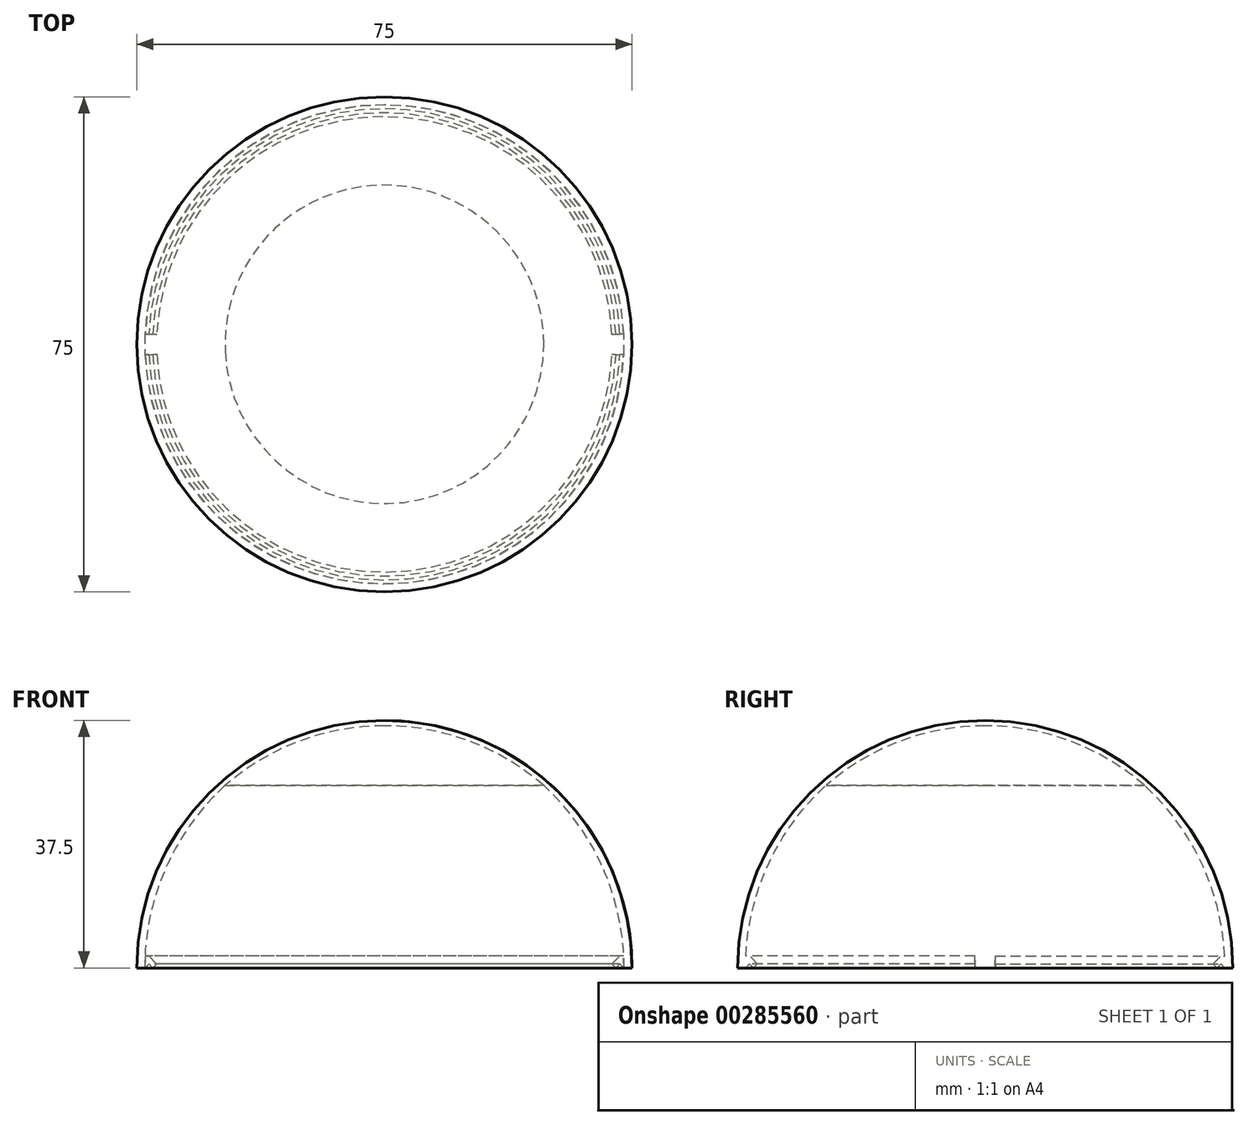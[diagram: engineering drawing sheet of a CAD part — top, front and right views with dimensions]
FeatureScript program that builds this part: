
annotation { "Feature Type Name" : "Feature", "Feature Type Description" : "" }
export const myFeature = defineFeature(function(context is Context, id is Id, definition is map)
    precondition{}
    {
        {
            var Q0;
            Q0=qCreatedBy(makeId("Front.planeOp"),FACE);
            var sketch = newSketch(context, id + "F0", { "sketchPlane" : qUnion([Q0])});
            skArc(sketch, "E0", {"start": v(0, 37.5) * mm, "mid": v(-26.52, 26.52) * mm, "end": v(-37.5, 0) * mm});
            skLineSegment(sketch, "E1", {"start": v(-37.5, 0) * mm, "end": v(-36.3, 0) * mm});
            skLineSegment(sketch, "E2", {"start": v(-36.3, 0) * mm, "end": v(-36.3, -8.57) * mm, "construction": true});
            skArc(sketch, "E3", {"start": v(-24.13, 27.65) * mm, "mid": v(-33.12, 15.1) * mm, "end": v(-36.3, 0) * mm});
            skLineSegment(sketch, "E4", {"start": v(0, 37.5) * mm, "end": v(0, 36.7) * mm});
            skLineSegment(sketch, "E5", {"start": v(-36.3, 0) * mm, "end": v(-35.7, 0.6) * mm});
            skLineSegment(sketch, "E6", {"start": v(-35.7, 0.6) * mm, "end": v(-35.1, 0) * mm});
            skLineSegment(sketch, "E7", {"start": v(-36.3, 0) * mm, "end": v(-35.1, 0) * mm, "construction": true});
            skPoint(sketch, "E8", {"position": v(-35.7, 0) * mm});
            skLineSegment(sketch, "E9", {"start": v(-34.5, 0.6) * mm, "end": v(-35.7, 1.8) * mm});
            skLineSegment(sketch, "E10", {"start": v(-35.7, 1.8) * mm, "end": v(-36.26, 1.8) * mm});
            skLineSegment(sketch, "E11", {"start": v(-34.5, 0.6) * mm, "end": v(-35.1, 0) * mm});
            skArc(sketch, "E12.trimOffspring", {"start": v(0, 36.7) * mm, "mid": v(-12.89, 34.36) * mm, "end": v(-24.13, 27.65) * mm});
            skSolve(sketch);
        }
        {
            var Q0;
            Q0 = qSketchRegion(id + "F0", true);
            var Q1;
            Q1=sQuery(id+"F0.wireOp",EDGE,"E4");
            revolve(context, id + "F1", {"entities" : qUnion([Q0]), "axis" : qUnion([Q1]), "revolveType" : RevolveType.FULL});
        }
        {
            var Q0;
            Q0=qCreatedBy(makeId("Front.planeOp"),FACE);
            var sketch = newSketch(context, id + "F2", { "sketchPlane" : qUnion([Q0])});
            skArc(sketch, "E13", {"start": v(-36.26, 1.8) * mm, "mid": v(-36.29, 0.9) * mm, "end": v(-36.3, 0) * mm});
            skLineSegment(sketch, "E14", {"start": v(-36.26, 1.8) * mm, "end": v(-34.5, 1.8) * mm});
            skLineSegment(sketch, "E15", {"start": v(-34.5, 1.8) * mm, "end": v(-34.5, 0) * mm});
            skLineSegment(sketch, "E16", {"start": v(-34.5, 0) * mm, "end": v(-36.3, 0) * mm});
            skLineSegment(sketch, "E17", {"start": v(0, 0) * mm, "end": v(0, 4.84) * mm, "construction": true});
            skLineSegment(sketch, "E18.MirrorCS", {"start": v(34.5, 0) * mm, "end": v(36.3, 0) * mm});
            skLineSegment(sketch, "E19.MirrorCS", {"start": v(36.26, 1.8) * mm, "end": v(34.5, 1.8) * mm});
            skLineSegment(sketch, "E20.MirrorCS", {"start": v(34.5, 1.8) * mm, "end": v(34.5, 0) * mm});
            skArc(sketch, "E21.MirrorCS", {"start": v(36.26, 1.8) * mm, "mid": v(36.29, 0.9) * mm, "end": v(36.3, 0) * mm});
            skSolve(sketch);
        }
        {
            var Q0;
            Q0 = qSketchRegion(id + "F2", true);
            var Q1;
            Q1=sQuery(id+"F2.wireOp",EDGE,"E17");
            revolve(context, id + "F3", {"operationType" : NewBodyOperationType.REMOVE, "entities" : qUnion([Q0]), "axis" : qUnion([Q1]), "revolveType" : RevolveType.SYMMETRIC, "angle" : 5 * degree});
        }
    });
